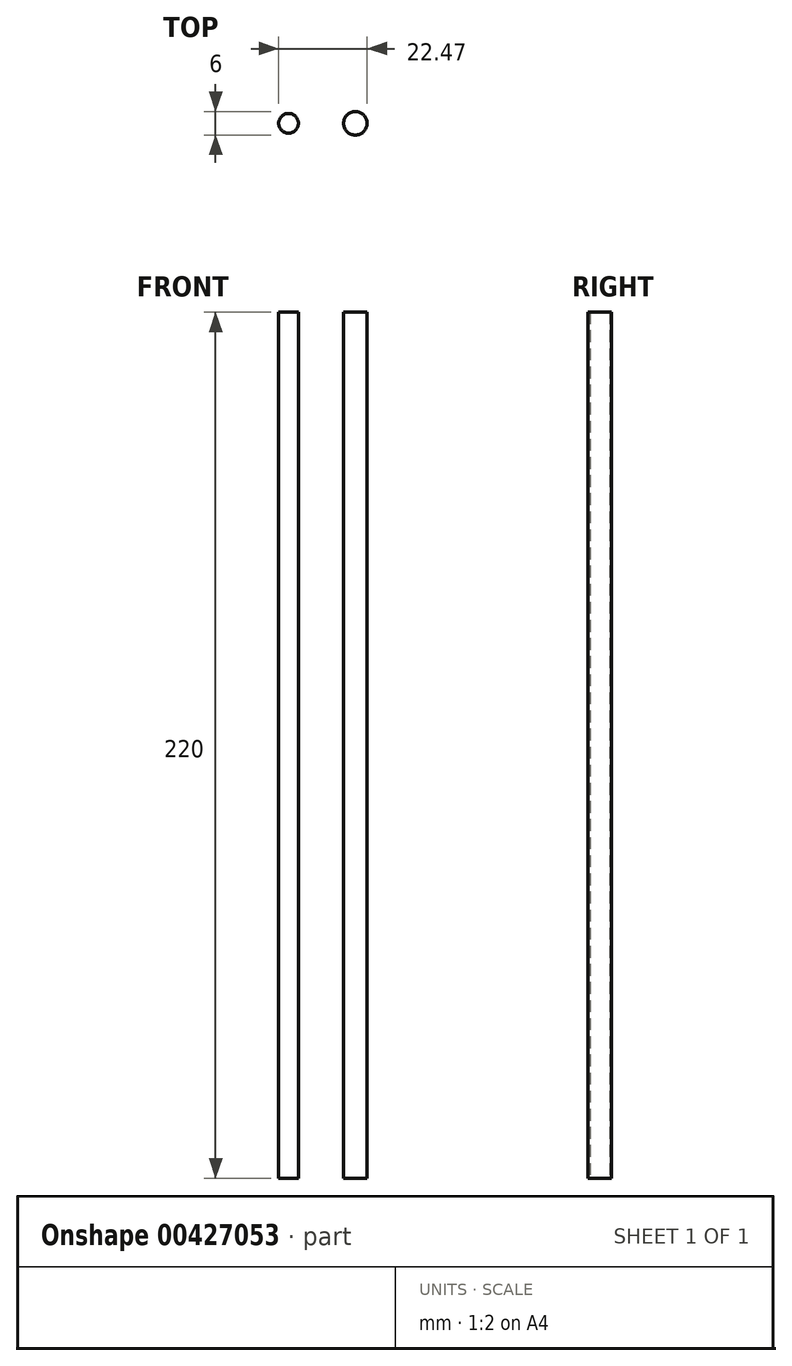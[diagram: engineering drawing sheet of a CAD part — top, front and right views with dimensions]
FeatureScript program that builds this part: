
annotation { "Feature Type Name" : "Feature", "Feature Type Description" : "" }
export const myFeature = defineFeature(function(context is Context, id is Id, definition is map)
    precondition{}
    {
        {
            var Q0;
            Q0=qCreatedBy(makeId("Top.planeOp"),FACE);
            var sketch = newSketch(context, id + "F0", { "sketchPlane" : qUnion([Q0])});
            skCircle(sketch, "E0", {"center": v(0, 0) * mm, "radius": 2.5 * mm});
            skCircle(sketch, "E1", {"center": v(16.97, 0) * mm, "radius": 3 * mm});
            skSolve(sketch);
        }
        {
            var Q0;
            Q0 = qSketchRegion(id + "F0", true);
            extrude(context, id + "F1", {"entities" : qUnion([Q0]), "depth" : 220 * mm});
        }
    });
